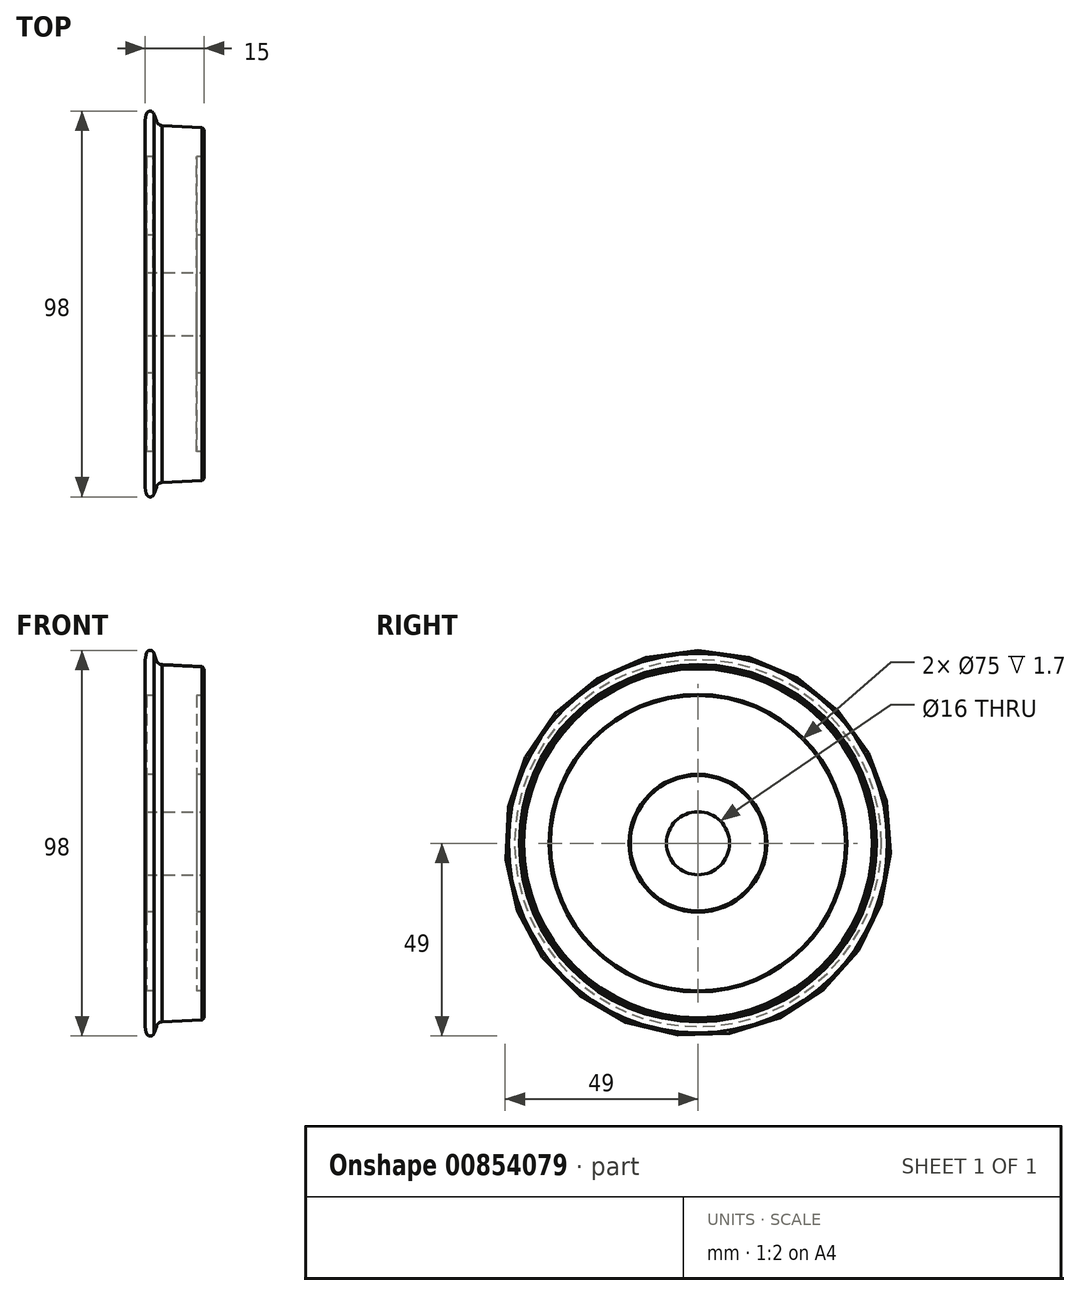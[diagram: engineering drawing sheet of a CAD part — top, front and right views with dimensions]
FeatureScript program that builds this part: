
annotation { "Feature Type Name" : "Feature", "Feature Type Description" : "" }
export const myFeature = defineFeature(function(context is Context, id is Id, definition is map)
    precondition{}
    {
        {
            var Q0;
            Q0=qCreatedBy(makeId("Top.planeOp"),FACE);
            var sketch = newSketch(context, id + "F0", { "sketchPlane" : qUnion([Q0])});
            skPoint(sketch, "E0", {"position": v(0, 0) * mm});
            skLineSegment(sketch, "E1", {"start": v(0, 0) * mm, "end": v(0, 46.6) * mm});
            skLineSegment(sketch, "E2", {"start": v(0, 46.6) * mm, "end": v(0.28, 48.17) * mm});
            skArc(sketch, "E3", {"start": v(0.28, 48.17) * mm, "mid": v(0.7, 48.82) * mm, "end": v(1.44, 48.98) * mm});
            skArc(sketch, "E4", {"start": v(1.44, 48.98) * mm, "mid": v(1.98, 48.7) * mm, "end": v(2.26, 48.17) * mm});
            skLineSegment(sketch, "E5", {"start": v(2.26, 48.17) * mm, "end": v(2.84, 46.48) * mm});
            skArc(sketch, "E6", {"start": v(2.84, 46.48) * mm, "mid": v(3.38, 45.7) * mm, "end": v(4.26, 45.35) * mm});
            skLineSegment(sketch, "E7", {"start": v(4.26, 45.35) * mm, "end": v(15, 44.83) * mm});
            skLineSegment(sketch, "E8", {"start": v(15, 44.83) * mm, "end": v(15, 37.5) * mm});
            skLineSegment(sketch, "E9", {"start": v(0, 0) * mm, "end": v(15, 0) * mm});
            skLineSegment(sketch, "E10.bottom", {"start": v(0, 17.5) * mm, "end": v(2, 17.5) * mm});
            skLineSegment(sketch, "E10.top", {"start": v(0, 37.5) * mm, "end": v(2, 37.5) * mm});
            skLineSegment(sketch, "E10.right", {"start": v(2, 17.5) * mm, "end": v(2, 37.5) * mm});
            skLineSegment(sketch, "E11.bottom", {"start": v(15, 17.5) * mm, "end": v(13, 17.5) * mm});
            skLineSegment(sketch, "E11.top", {"start": v(15, 37.5) * mm, "end": v(13, 37.5) * mm});
            skLineSegment(sketch, "E11.left", {"start": v(15, 17.5) * mm, "end": v(15, 17.5) * mm});
            skLineSegment(sketch, "E11.right", {"start": v(13, 17.5) * mm, "end": v(13, 37.5) * mm});
            skLineSegment(sketch, "E12", {"start": v(15, 37.5) * mm, "end": v(15, 0) * mm});
            skLineSegment(sketch, "E13", {"start": v(15, 17.5) * mm, "end": v(15, 37.5) * mm});
            skSolve(sketch);
        }
        {
            var Q0;
            Q0=makeQuery(id+"F0.imprint","IMPRINT",FACE,{"disambiguationData":[TD([[makeQuery(id+"F0.imprint","IMPRINT",EDGE,{"derivedFrom":sQuery(id+"F0.wireOp",EDGE,"E1")}),-1.0]])]});
            var Q1;
            Q1=sQuery(id+"F0.wireOp",EDGE,"E9");
            revolve(context, id + "F1", {"surfaceOperationType" : NewSurfaceOperationType.NEW, "entities" : qUnion([Q0]), "axis" : qUnion([Q1]), "revolveType" : RevolveType.FULL});
        }
        {
            var Q0;
            Q0=makeQuery(id+"F1.opRevolve","SWEPT_EDGE",EDGE,{"disambiguationData":[OSD([sQuery(id+"F0.wireOp",EDGE,"E7"),sQuery(id+"F0.wireOp",EDGE,"E8")])]});
            chamfer(context, id + "F2", {"entities" : qUnion([Q0]), "width" : 0.5 * mm, "tangentPropagation" : true});
        }
        {
            var Q0;
            Q0=qCreatedBy(makeId("Right.planeOp"),FACE);
            var sketch = newSketch(context, id + "F3", { "sketchPlane" : qUnion([Q0])});
            skPoint(sketch, "E14", {"position": v(0, 0) * mm});
            skSolve(sketch);
        }
        {
            var Q0;
            Q0=sQuery(id+"F3.wireOp",VERTEX,"E14");
            var Q1;
            Q1=makeQuery(id+"F1.opRevolve","SWEPT_BODY",BODY,{"disambiguationData":[OSD([sQuery(id+"F0.wireOp",EDGE,"E1"),sQuery(id+"F0.wireOp",EDGE,"E2"),sQuery(id+"F0.wireOp",EDGE,"E3"),sQuery(id+"F0.wireOp",EDGE,"E4"),sQuery(id+"F0.wireOp",EDGE,"E5"),sQuery(id+"F0.wireOp",EDGE,"E6"),sQuery(id+"F0.wireOp",EDGE,"E7"),sQuery(id+"F0.wireOp",EDGE,"E8"),sQuery(id+"F0.wireOp",EDGE,"E9")])]});
            hole(context, id + "F4", {"style" : HoleStyle.SIMPLE, "endStyle" : HoleEndStyle.THROUGH, "oppositeDirection" : true, "holeDiameter" : 16 * mm, "majorDiameter" : 5 * mm, "isTappedThrough" : true, "tappedDepth" : 12 * mm, "tapClearance" : 3, "locations" : qUnion([Q0]), "scope" : qUnion([Q1]), "startStyle" : HoleStartStyle.PART});
        }
        {
            var Q0;
            Q0=makeQuery(id+"F1.opRevolve","SWEPT_EDGE",EDGE,{"disambiguationData":[OSD([sQuery(id+"F0.wireOp",EDGE,"E8"),sQuery(id+"F0.wireOp",EDGE,"E11.top"),sQuery(id+"F0.wireOp",EDGE,"E13")])]});
            var Q1;
            Q1=makeQuery(id+"F1.opRevolve","SWEPT_EDGE",EDGE,{"disambiguationData":[OSD([sQuery(id+"F0.wireOp",EDGE,"E11.bottom"),sQuery(id+"F0.wireOp",EDGE,"E12"),sQuery(id+"F0.wireOp",EDGE,"E13")])]});
            var Q2;
            Q2=makeQuery(id+"F1.opRevolve","SWEPT_EDGE",EDGE,{"disambiguationData":[OSD([sQuery(id+"F0.wireOp",EDGE,"E1"),sQuery(id+"F0.wireOp",EDGE,"E10.bottom")])]});
            var Q3;
            Q3=makeQuery(id+"F1.opRevolve","SWEPT_EDGE",EDGE,{"disambiguationData":[OSD([sQuery(id+"F0.wireOp",EDGE,"E1"),sQuery(id+"F0.wireOp",EDGE,"E10.top")])]});
            chamfer(context, id + "F5", {"entities" : qUnion([Q0, Q1, Q2, Q3]), "width" : 0.3 * mm, "tangentPropagation" : true});
        }
    });
